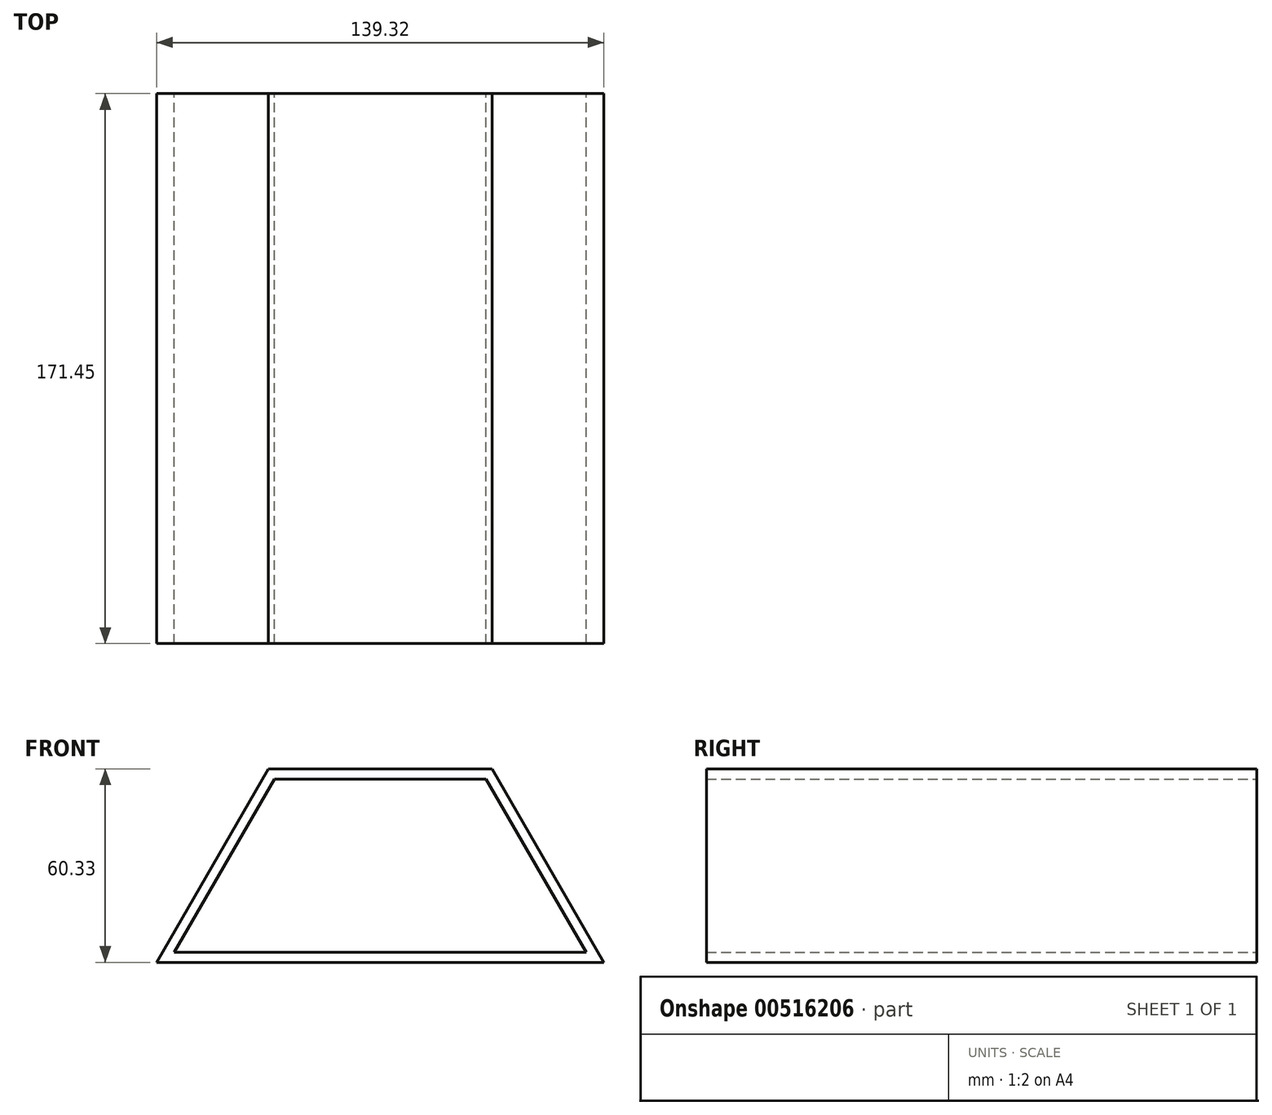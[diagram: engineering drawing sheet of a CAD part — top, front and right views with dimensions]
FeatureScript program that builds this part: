
annotation { "Feature Type Name" : "Feature", "Feature Type Description" : "" }
export const myFeature = defineFeature(function(context is Context, id is Id, definition is map)
    precondition{}
    {
        {
            var Q0;
            Q0=qCreatedBy(makeId("Front.planeOp"),FACE);
            var sketch = newSketch(context, id + "F0", { "sketchPlane" : qUnion([Q0])});
            skCircle(sketch, "E0.cCircle", {"center": v(0, 0) * mm, "radius": 60.32 * mm, "construction": true});
            skLineSegment(sketch, "E0.0", {"start": v(-34.83, 60.33) * mm, "end": v(34.83, 60.33) * mm});
            skLineSegment(sketch, "E0.1", {"start": v(34.83, 60.33) * mm, "end": v(69.66, 0) * mm});
            skLineSegment(sketch, "E0.2", {"start": v(69.66, 0) * mm, "end": v(34.83, -60.32) * mm});
            skLineSegment(sketch, "E0.3", {"start": v(34.83, -60.32) * mm, "end": v(-34.83, -60.33) * mm});
            skLineSegment(sketch, "E0.4", {"start": v(-34.83, -60.32) * mm, "end": v(-69.66, 0) * mm});
            skLineSegment(sketch, "E0.5", {"start": v(-69.66, 0) * mm, "end": v(-34.83, 60.32) * mm});
            skPoint(sketch, "E0.0.midPoint", {"position": v(0, 60.33) * mm});
            skLineSegment(sketch, "E1", {"start": v(-69.66, 0) * mm, "end": v(69.66, 0) * mm});
            skLineSegment(sketch, "E2.0", {"start": v(-33, 57.15) * mm, "end": v(33, 57.15) * mm});
            skLineSegment(sketch, "E2.1", {"start": v(-64.16, 3.17) * mm, "end": v(-33, 57.15) * mm});
            skLineSegment(sketch, "E2.2", {"start": v(-64.16, 3.18) * mm, "end": v(64.16, 3.18) * mm});
            skLineSegment(sketch, "E2.3", {"start": v(33, 57.15) * mm, "end": v(64.16, 3.18) * mm});
            skSolve(sketch);
        }
        {
            var Q0;
            Q0=makeQuery(id+"F0.imprint","IMPRINT",FACE,{"disambiguationData":[TD([[makeQuery(id+"F0.imprint","IMPRINT",EDGE,{"derivedFrom":sQuery(id+"F0.wireOp",EDGE,"E0.0")}),-1.0]])]});
            extrude(context, id + "F1", {"entities" : qUnion([Q0]), "depth" : 171.45 * mm, "offsetDistance" : 25.4 * mm});
        }
    });
